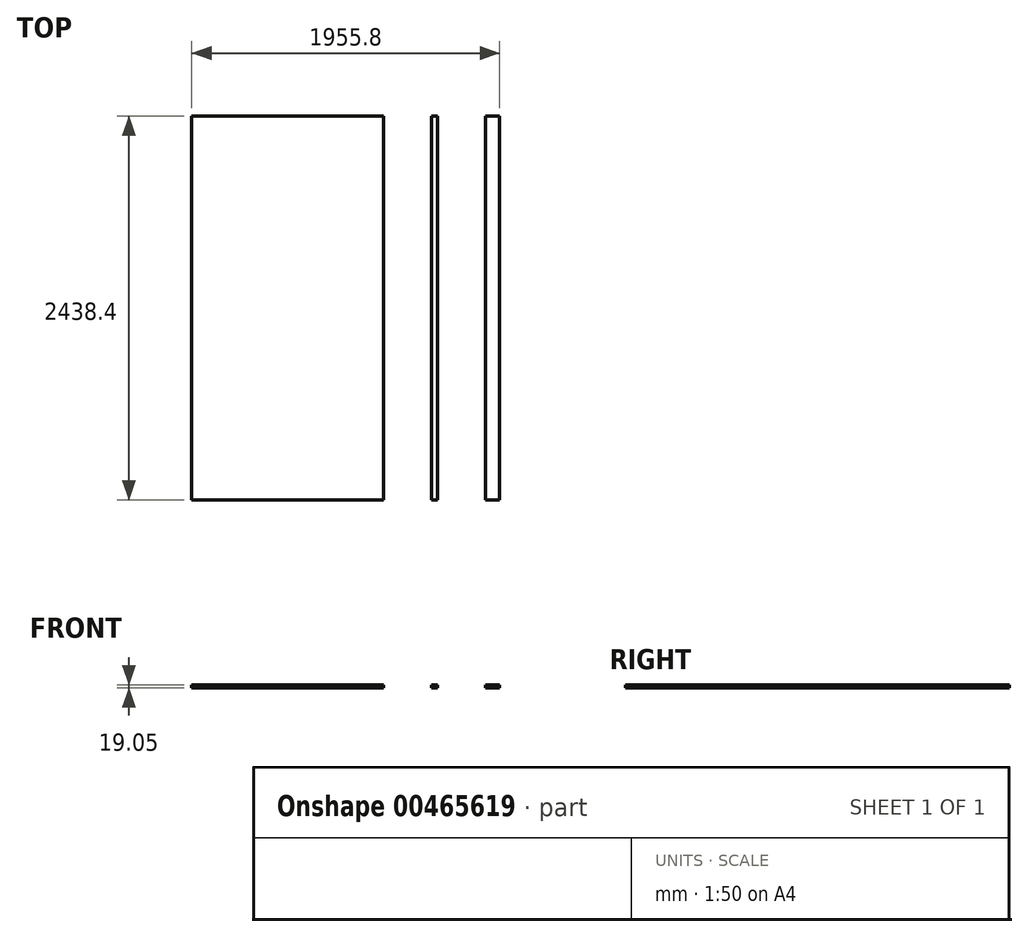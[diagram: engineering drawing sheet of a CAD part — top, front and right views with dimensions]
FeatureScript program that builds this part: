
annotation { "Feature Type Name" : "Feature", "Feature Type Description" : "" }
export const myFeature = defineFeature(function(context is Context, id is Id, definition is map)
    precondition{}
    {
        {
            var Q0;
            Q0=qCreatedBy(makeId("Top.planeOp"),FACE);
            var sketch = newSketch(context, id + "F0", { "sketchPlane" : qUnion([Q0])});
            skLineSegment(sketch, "E0.bottom", {"start": v(0, 0) * mm, "end": v(1219.2, 0) * mm});
            skLineSegment(sketch, "E0.top", {"start": v(0, 2438.4) * mm, "end": v(1219.2, 2438.4) * mm});
            skLineSegment(sketch, "E0.left", {"start": v(0, 0) * mm, "end": v(0, 2438.4) * mm});
            skLineSegment(sketch, "E0.right", {"start": v(1219.2, 0) * mm, "end": v(1219.2, 2438.4) * mm});
            skLineSegment(sketch, "E1.bottom", {"start": v(1524, 0) * mm, "end": v(1562.1, 0) * mm});
            skLineSegment(sketch, "E1.top", {"start": v(1524, 2438.4) * mm, "end": v(1562.1, 2438.4) * mm});
            skLineSegment(sketch, "E1.left", {"start": v(1524, 0) * mm, "end": v(1524, 2438.4) * mm});
            skLineSegment(sketch, "E1.right", {"start": v(1562.1, 0) * mm, "end": v(1562.1, 2438.4) * mm});
            skLineSegment(sketch, "E2.bottom", {"start": v(1866.9, 0) * mm, "end": v(1955.8, 0) * mm});
            skLineSegment(sketch, "E2.top", {"start": v(1866.9, 2438.4) * mm, "end": v(1955.8, 2438.4) * mm});
            skLineSegment(sketch, "E2.left", {"start": v(1866.9, 0) * mm, "end": v(1866.9, 2438.4) * mm});
            skLineSegment(sketch, "E2.right", {"start": v(1955.8, 0) * mm, "end": v(1955.8, 2438.4) * mm});
            skSolve(sketch);
        }
        {
            var Q0;
            Q0 = qSketchRegion(id + "F0", true);
            extrude(context, id + "F1", {"entities" : qUnion([Q0]), "depth" : 19.05 * mm});
        }
    });
